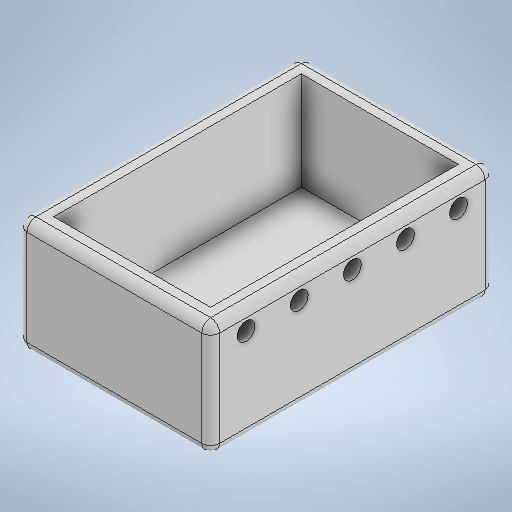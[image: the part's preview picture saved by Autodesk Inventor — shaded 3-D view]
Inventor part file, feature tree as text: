
AUTODESK INVENTOR PART (.ipt)
format: ipt  version: 2025 (Build 290162000, 162)  size: 268,288 bytes
history: native  units: in
note: dims shown in document units (in); Inventor stores cm internally (conversion verified against a paired STEP export)
features: extrude x3, sketch x3, fillet x1
ambient origin geometry x8: Origin, YZ Plane, XZ Plane, XY Plane, X Axis, Y Axis, Z Axis, Center Point
bodies: Solid1 (feature_tree)
feature tree (7):
  extrude  "Extrusion1"  Depth=5.0in
  fillet  "Fillet1"  Radius=12.5in
  extrude  "Extrusion4"  Depth=0.3937in
  extrude  "Extrusion5"  Depth=0.3937in
  sketch  "Sketch1"  dims[d0=8.5in d1=5.0in d2=12.5in d3=0.0in]
  sketch  "Sketch4"  dims[d4=0.3937in d20=0.3937in]
  sketch  "Sketch5"  dims[d21=0.3937in d22=0.3937in d23=0.3937in d24=4.3307in d25=0.0in d26=0.7874in d27=0.7874in d28=0.7874in d29=0.7874in d30=0.7874in d31=1.1713in d32=2.3425in d33=2.3425in d34=2.3425in d35=2.3425in d36=2.3425in d37=0.0in d5=0.0344in]
